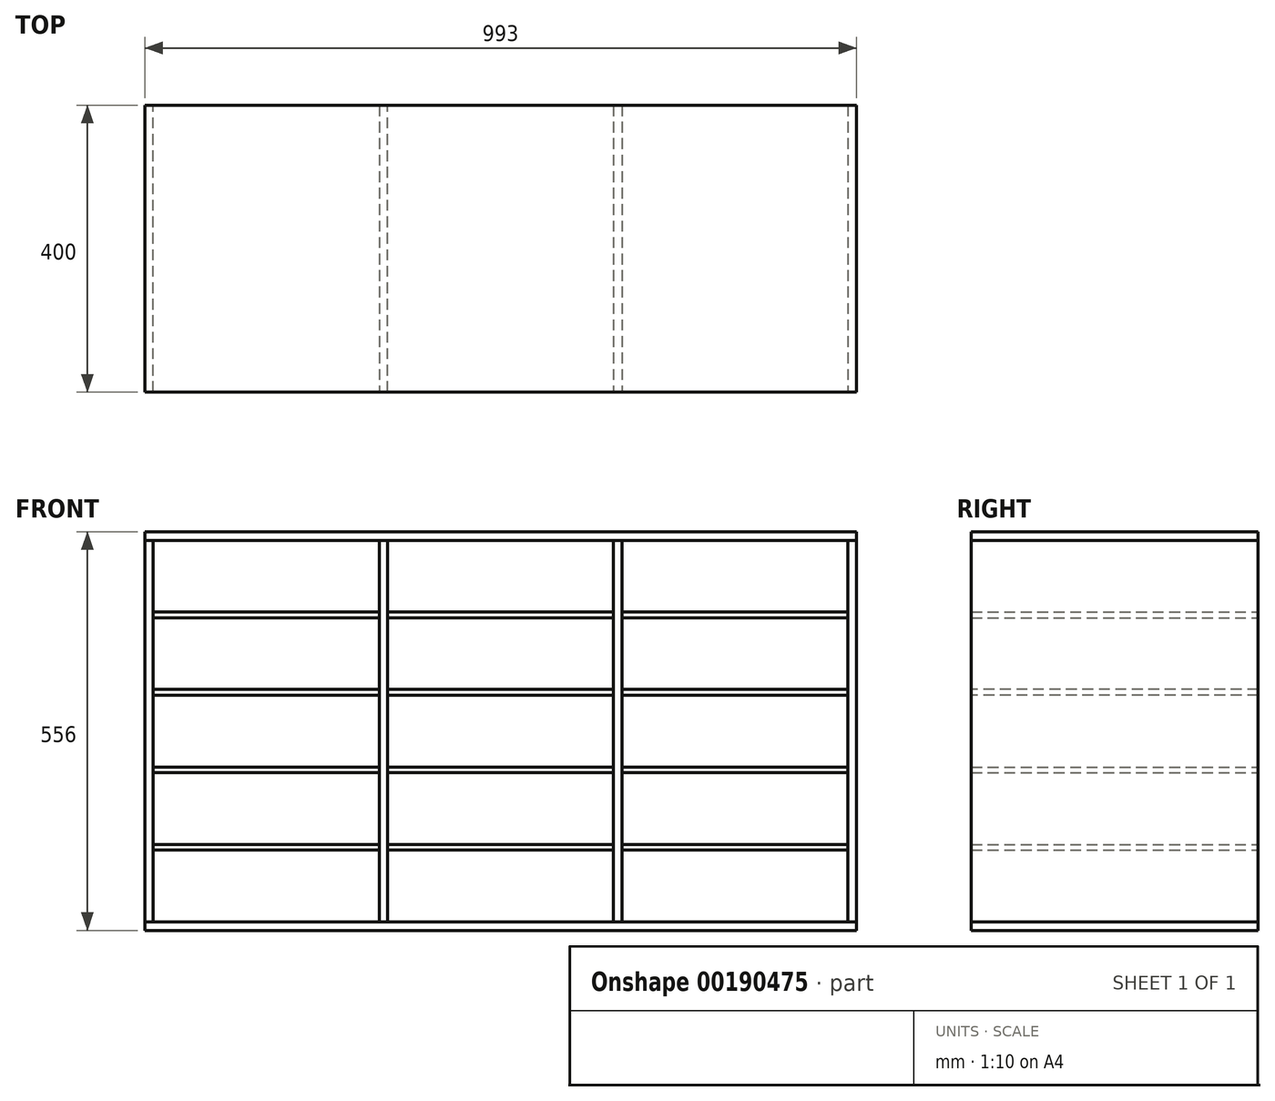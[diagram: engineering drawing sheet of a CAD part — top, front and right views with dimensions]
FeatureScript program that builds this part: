
annotation { "Feature Type Name" : "Feature", "Feature Type Description" : "" }
export const myFeature = defineFeature(function(context is Context, id is Id, definition is map)
    precondition{}
    {
        {
            var Q0;
            Q0=qCreatedBy(makeId("Top.planeOp"),FACE);
            var sketch = newSketch(context, id + "F0", { "sketchPlane" : qUnion([Q0])});
            skLineSegment(sketch, "E0.bottom", {"start": v(-496.5, 200) * mm, "end": v(496.5, 200) * mm});
            skLineSegment(sketch, "E0.top", {"start": v(-496.5, -200) * mm, "end": v(496.5, -200) * mm});
            skLineSegment(sketch, "E0.left", {"start": v(-496.5, 200) * mm, "end": v(-496.5, -200) * mm});
            skLineSegment(sketch, "E0.right", {"start": v(496.5, 200) * mm, "end": v(496.5, -200) * mm});
            skPoint(sketch, "E0.middle", {"position": v(0, 0) * mm});
            skSolve(sketch);
        }
        {
            var Q0;
            Q0 = qSketchRegion(id + "F0", true);
            extrude(context, id + "F1", {"entities" : qUnion([Q0]), "depth" : 12 * mm});
        }
        {
            var Q0;
            Q0=makeQuery(id+"F1.opExtrude","CAP_FACE",FACE,{"disambiguationData":[OSD([sQuery(id+"F0.wireOp",EDGE,"E0.bottom"),sQuery(id+"F0.wireOp",EDGE,"E0.top"),sQuery(id+"F0.wireOp",EDGE,"E0.left"),sQuery(id+"F0.wireOp",EDGE,"E0.right")])],"isStart":false});
            var sketch = newSketch(context, id + "F2", { "sketchPlane" : qUnion([Q0])});
            skLineSegment(sketch, "E1.bottom", {"start": v(-496.5, -200) * mm, "end": v(-484.5, -200) * mm});
            skLineSegment(sketch, "E1.top", {"start": v(-496.5, 200) * mm, "end": v(-484.5, 200) * mm});
            skLineSegment(sketch, "E1.left", {"start": v(-496.5, -200) * mm, "end": v(-496.5, 200) * mm});
            skLineSegment(sketch, "E1.right", {"start": v(-484.5, -200) * mm, "end": v(-484.5, 200) * mm});
            skLineSegment(sketch, "E2.bottom", {"start": v(496.5, -200) * mm, "end": v(484.5, -200) * mm});
            skLineSegment(sketch, "E2.top", {"start": v(496.5, 200) * mm, "end": v(484.5, 200) * mm});
            skLineSegment(sketch, "E2.left", {"start": v(496.5, -200) * mm, "end": v(496.5, 200) * mm});
            skLineSegment(sketch, "E2.right", {"start": v(484.5, -200) * mm, "end": v(484.5, 200) * mm});
            skSolve(sketch);
        }
        {
            var Q0;
            Q0 = qSketchRegion(id + "F2", true);
            extrude(context, id + "F3", {"entities" : qUnion([Q0]), "depth" : (600 - 24 - 44) * mm});
        }
        {
            var Q0;
            Q0=makeQuery(id+"F3.opExtrude","CAP_FACE",FACE,{"disambiguationData":[OSD([sQuery(id+"F2.wireOp",EDGE,"E1.bottom"),sQuery(id+"F2.wireOp",EDGE,"E1.top"),sQuery(id+"F2.wireOp",EDGE,"E1.left"),sQuery(id+"F2.wireOp",EDGE,"E1.right")])],"isStart":false});
            var sketch = newSketch(context, id + "F4", { "sketchPlane" : qUnion([Q0])});
            skLineSegment(sketch, "E3.bottom", {"start": v(-496.5, 200) * mm, "end": v(496.5, 200) * mm});
            skLineSegment(sketch, "E3.top", {"start": v(-496.5, -200) * mm, "end": v(496.5, -200) * mm});
            skLineSegment(sketch, "E3.left", {"start": v(-496.5, 200) * mm, "end": v(-496.5, -200) * mm});
            skLineSegment(sketch, "E3.right", {"start": v(496.5, 200) * mm, "end": v(496.5, -200) * mm});
            skSolve(sketch);
        }
        {
            var Q0;
            Q0 = qSketchRegion(id + "F4", true);
            extrude(context, id + "F5", {"entities" : qUnion([Q0]), "depth" : 12 * mm});
        }
        {
            var Q0;
            Q0=makeQuery(id+"F1.opExtrude","CAP_FACE",FACE,{"disambiguationData":[OSD([sQuery(id+"F0.wireOp",EDGE,"E0.bottom"),sQuery(id+"F0.wireOp",EDGE,"E0.top"),sQuery(id+"F0.wireOp",EDGE,"E0.left"),sQuery(id+"F0.wireOp",EDGE,"E0.right")])],"isStart":false});
            var sketch = newSketch(context, id + "F6", { "sketchPlane" : qUnion([Q0])});
            skLineSegment(sketch, "E4.bottom", {"start": v(-169.5, 200) * mm, "end": v(-157.5, 200) * mm});
            skLineSegment(sketch, "E4.top", {"start": v(-169.5, -200) * mm, "end": v(-157.5, -200) * mm});
            skLineSegment(sketch, "E4.left", {"start": v(-169.5, 200) * mm, "end": v(-169.5, -200) * mm});
            skLineSegment(sketch, "E4.right", {"start": v(-157.5, 200) * mm, "end": v(-157.5, -200) * mm});
            skLineSegment(sketch, "E5.bottom", {"start": v(157.5, 200) * mm, "end": v(169.5, 200) * mm});
            skLineSegment(sketch, "E5.top", {"start": v(157.5, -200) * mm, "end": v(169.5, -200) * mm});
            skLineSegment(sketch, "E5.left", {"start": v(157.5, 200) * mm, "end": v(157.5, -200) * mm});
            skLineSegment(sketch, "E5.right", {"start": v(169.5, 200) * mm, "end": v(169.5, -200) * mm});
            skSolve(sketch);
        }
        {
            var Q0;
            Q0 = qSketchRegion(id + "F6", true);
            extrude(context, id + "F7", {"entities" : qUnion([Q0]), "depth" : (600 - 24 - 44) * mm});
        }
        {
            var Q0;
            Q0=makeQuery(id+"F3.opExtrude","SWEPT_FACE",FACE,{"disambiguationData":[OSD([sQuery(id+"F2.wireOp",EDGE,"E2.right")])]});
            var sketch = newSketch(context, id + "F8", { "sketchPlane" : qUnion([Q0])});
            skLineSegment(sketch, "E6.bottom", {"start": v(-200, 120) * mm, "end": v(200, 120) * mm});
            skLineSegment(sketch, "E6.top", {"start": v(-200, 112) * mm, "end": v(200, 112) * mm});
            skLineSegment(sketch, "E6.left", {"start": v(-200, 120) * mm, "end": v(-200, 112) * mm});
            skLineSegment(sketch, "E6.right", {"start": v(200, 120) * mm, "end": v(200, 112) * mm});
            skLineSegment(sketch, "E7.bottom", {"start": v(-200, 228) * mm, "end": v(200, 228) * mm});
            skLineSegment(sketch, "E7.top", {"start": v(-200, 220) * mm, "end": v(200, 220) * mm});
            skLineSegment(sketch, "E7.left", {"start": v(-200, 228) * mm, "end": v(-200, 220) * mm});
            skLineSegment(sketch, "E7.right", {"start": v(200, 228) * mm, "end": v(200, 220) * mm});
            skLineSegment(sketch, "E8.bottom", {"start": v(-200, 336) * mm, "end": v(200, 336) * mm});
            skLineSegment(sketch, "E8.top", {"start": v(-200, 328) * mm, "end": v(200, 328) * mm});
            skLineSegment(sketch, "E8.left", {"start": v(-200, 336) * mm, "end": v(-200, 328) * mm});
            skLineSegment(sketch, "E8.right", {"start": v(200, 336) * mm, "end": v(200, 328) * mm});
            skLineSegment(sketch, "E9.bottom", {"start": v(-200, 444) * mm, "end": v(200, 444) * mm});
            skLineSegment(sketch, "E9.top", {"start": v(-200, 436) * mm, "end": v(200, 436) * mm});
            skLineSegment(sketch, "E9.left", {"start": v(-200, 444) * mm, "end": v(-200, 436) * mm});
            skLineSegment(sketch, "E9.right", {"start": v(200, 444) * mm, "end": v(200, 436) * mm});
            skSolve(sketch);
        }
        {
            var Q0;
            Q0 = qSketchRegion(id + "F8", true);
            extrude(context, id + "F9", {"entities" : qUnion([Q0]), "depth" : 315 * mm});
        }
        {
            var Q0;
            Q0=makeQuery(id+"F7.opExtrude","SWEPT_FACE",FACE,{"disambiguationData":[OSD([sQuery(id+"F6.wireOp",EDGE,"E4.left")])]});
            var sketch = newSketch(context, id + "F10", { "sketchPlane" : qUnion([Q0])});
            skLineSegment(sketch, "E10.bottom", {"start": v(-200, 112) * mm, "end": v(200, 112) * mm});
            skLineSegment(sketch, "E10.top", {"start": v(-200, 120) * mm, "end": v(200, 120) * mm});
            skLineSegment(sketch, "E10.left", {"start": v(-200, 120) * mm, "end": v(-200, 112) * mm});
            skLineSegment(sketch, "E10.right", {"start": v(200, 120) * mm, "end": v(200, 112) * mm});
            skLineSegment(sketch, "E11.bottom", {"start": v(-200, 228) * mm, "end": v(200, 228) * mm});
            skLineSegment(sketch, "E11.top", {"start": v(-200, 220) * mm, "end": v(200, 220) * mm});
            skLineSegment(sketch, "E11.left", {"start": v(-200, 228) * mm, "end": v(-200, 220) * mm});
            skLineSegment(sketch, "E11.right", {"start": v(200, 228) * mm, "end": v(200, 220) * mm});
            skLineSegment(sketch, "E12.bottom", {"start": v(-200, 336) * mm, "end": v(200, 336) * mm});
            skLineSegment(sketch, "E12.top", {"start": v(-200, 328) * mm, "end": v(200, 328) * mm});
            skLineSegment(sketch, "E12.left", {"start": v(-200, 336) * mm, "end": v(-200, 328) * mm});
            skLineSegment(sketch, "E12.right", {"start": v(200, 336) * mm, "end": v(200, 328) * mm});
            skLineSegment(sketch, "E13.bottom", {"start": v(-200, 444) * mm, "end": v(200, 444) * mm});
            skLineSegment(sketch, "E13.top", {"start": v(-200, 436) * mm, "end": v(200, 436) * mm});
            skLineSegment(sketch, "E13.left", {"start": v(-200, 444) * mm, "end": v(-200, 436) * mm});
            skLineSegment(sketch, "E13.right", {"start": v(200, 444) * mm, "end": v(200, 436) * mm});
            skSolve(sketch);
        }
        {
            var Q0;
            Q0 = qSketchRegion(id + "F10", true);
            extrude(context, id + "F11", {"entities" : qUnion([Q0]), "depth" : 315 * mm});
        }
        {
            var Q0;
            Q0=makeQuery(id+"F7.opExtrude","SWEPT_FACE",FACE,{"disambiguationData":[OSD([sQuery(id+"F6.wireOp",EDGE,"E4.right")])]});
            var sketch = newSketch(context, id + "F12", { "sketchPlane" : qUnion([Q0])});
            skLineSegment(sketch, "E14.bottom", {"start": v(-200, 120) * mm, "end": v(200, 120) * mm});
            skLineSegment(sketch, "E14.top", {"start": v(-200, 112) * mm, "end": v(200, 112) * mm});
            skLineSegment(sketch, "E14.left", {"start": v(-200, 120) * mm, "end": v(-200, 112) * mm});
            skLineSegment(sketch, "E14.right", {"start": v(200, 120) * mm, "end": v(200, 112) * mm});
            skLineSegment(sketch, "E15.bottom", {"start": v(-200, 228) * mm, "end": v(200, 228) * mm});
            skLineSegment(sketch, "E15.top", {"start": v(-200, 220) * mm, "end": v(200, 220) * mm});
            skLineSegment(sketch, "E15.left", {"start": v(-200, 228) * mm, "end": v(-200, 220) * mm});
            skLineSegment(sketch, "E15.right", {"start": v(200, 228) * mm, "end": v(200, 220) * mm});
            skLineSegment(sketch, "E16.bottom", {"start": v(-200, 336) * mm, "end": v(200, 336) * mm});
            skLineSegment(sketch, "E16.top", {"start": v(-200, 328) * mm, "end": v(200, 328) * mm});
            skLineSegment(sketch, "E16.left", {"start": v(-200, 336) * mm, "end": v(-200, 328) * mm});
            skLineSegment(sketch, "E16.right", {"start": v(200, 336) * mm, "end": v(200, 328) * mm});
            skLineSegment(sketch, "E17.bottom", {"start": v(-200, 444) * mm, "end": v(200, 444) * mm});
            skLineSegment(sketch, "E17.top", {"start": v(-200, 436) * mm, "end": v(200, 436) * mm});
            skLineSegment(sketch, "E17.left", {"start": v(-200, 444) * mm, "end": v(-200, 436) * mm});
            skLineSegment(sketch, "E17.right", {"start": v(200, 444) * mm, "end": v(200, 436) * mm});
            skSolve(sketch);
        }
        {
            var Q0;
            Q0 = qSketchRegion(id + "F12", true);
            extrude(context, id + "F13", {"entities" : qUnion([Q0]), "depth" : 315 * mm});
        }
    });
